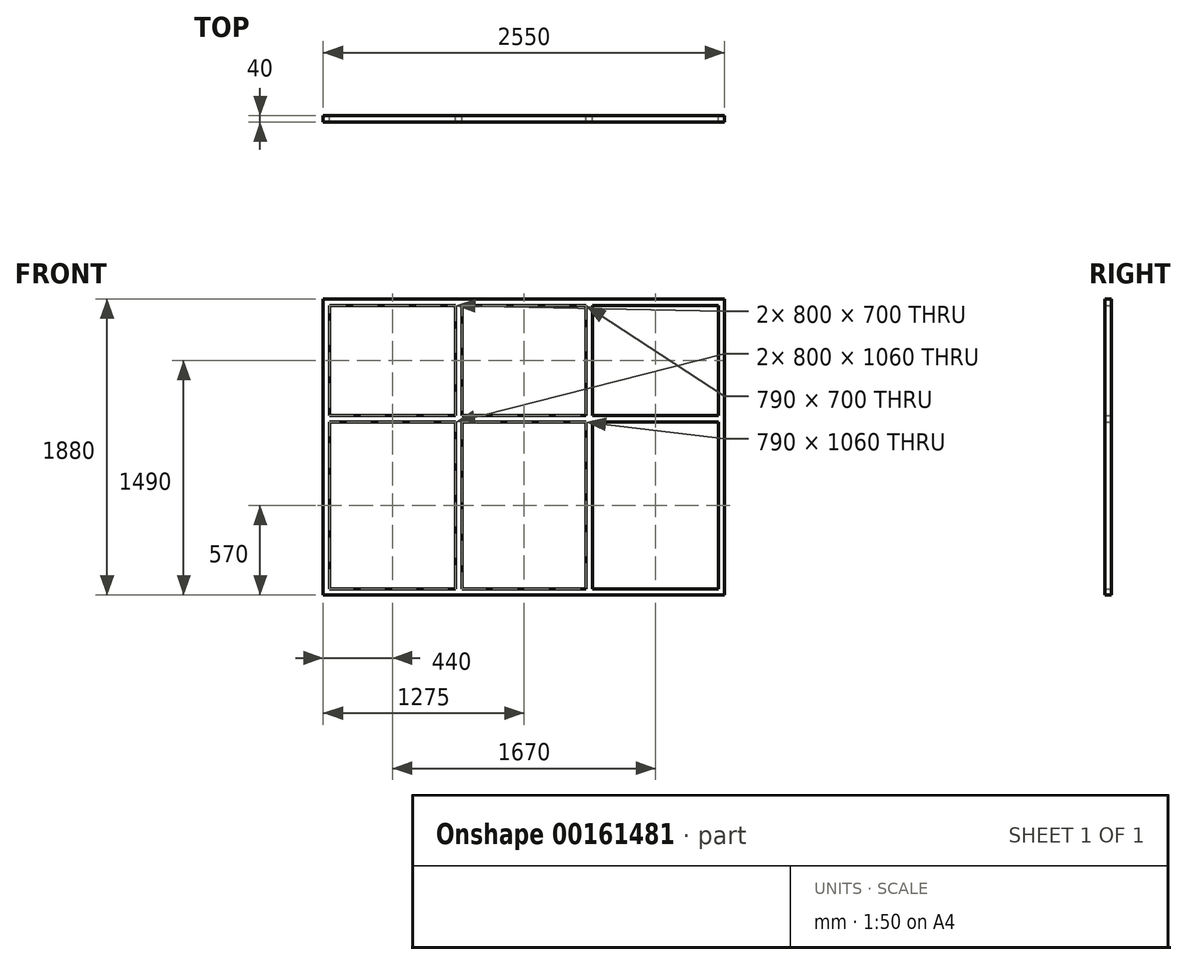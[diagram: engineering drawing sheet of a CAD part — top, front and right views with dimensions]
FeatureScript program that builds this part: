
annotation { "Feature Type Name" : "Feature", "Feature Type Description" : "" }
export const myFeature = defineFeature(function(context is Context, id is Id, definition is map)
    precondition{}
    {
        {
            var Q0;
            Q0=qCreatedBy(makeId("Front.planeOp"),FACE);
            var sketch = newSketch(context, id + "F0", { "sketchPlane" : qUnion([Q0])});
            skLineSegment(sketch, "E0.bottom", {"start": v(-1235, 900) * mm, "end": v(-435, 900) * mm});
            skLineSegment(sketch, "E0.top", {"start": v(-1235, -900) * mm, "end": v(-435, -900) * mm});
            skLineSegment(sketch, "E0.left", {"start": v(-1235, 900) * mm, "end": v(-1235, 200) * mm});
            skLineSegment(sketch, "E0.right", {"start": v(1235, 900) * mm, "end": v(1235, 200) * mm});
            skPoint(sketch, "E0.middle", {"position": v(0, 0) * mm});
            skLineSegment(sketch, "E1.bottom", {"start": v(-1275, 940) * mm, "end": v(1275, 940) * mm});
            skLineSegment(sketch, "E1.top", {"start": v(-1275, -940) * mm, "end": v(1275, -940) * mm});
            skLineSegment(sketch, "E1.left", {"start": v(-1275, 940) * mm, "end": v(-1275, -940) * mm});
            skLineSegment(sketch, "E1.right", {"start": v(1275, 940) * mm, "end": v(1275, -940) * mm});
            skLineSegment(sketch, "E2.left", {"start": v(-435, 900) * mm, "end": v(-435, 200) * mm});
            skLineSegment(sketch, "E2.right", {"start": v(-395, 900) * mm, "end": v(-395, 200) * mm});
            skLineSegment(sketch, "E3.left", {"start": v(395, 900) * mm, "end": v(395, 200) * mm});
            skLineSegment(sketch, "E3.right", {"start": v(435, 900) * mm, "end": v(435, 200) * mm});
            skLineSegment(sketch, "E4.trimOffspring", {"start": v(-395, 900) * mm, "end": v(395, 900) * mm});
            skLineSegment(sketch, "E5.trimOffspring", {"start": v(-395, -900) * mm, "end": v(395, -900) * mm});
            skLineSegment(sketch, "E6.trimOffspring", {"start": v(435, 900) * mm, "end": v(1235, 900) * mm});
            skLineSegment(sketch, "E7.trimOffspring", {"start": v(435, -900) * mm, "end": v(1235, -900) * mm});
            skLineSegment(sketch, "E8.bottom", {"start": v(-1235, 200) * mm, "end": v(-435, 200) * mm});
            skLineSegment(sketch, "E8.top", {"start": v(-1235, 160) * mm, "end": v(-435, 160) * mm});
            skLineSegment(sketch, "E9.trimOffspring", {"start": v(-435, 160) * mm, "end": v(-435, -900) * mm});
            skLineSegment(sketch, "E10.trimOffspring", {"start": v(-1235, 160) * mm, "end": v(-1235, -900) * mm});
            skLineSegment(sketch, "E11", {"start": v(-395, 200) * mm, "end": v(395, 200) * mm});
            skLineSegment(sketch, "E12", {"start": v(-395, 160) * mm, "end": v(395, 160) * mm});
            skLineSegment(sketch, "E13.trimOffspring", {"start": v(-395, 160) * mm, "end": v(-395, -900) * mm});
            skLineSegment(sketch, "E14.trimOffspring", {"start": v(395, 160) * mm, "end": v(395, -900) * mm});
            skLineSegment(sketch, "E15.trimOffspring", {"start": v(435, 200) * mm, "end": v(1235, 200) * mm});
            skLineSegment(sketch, "E16.trimOffspring", {"start": v(435, 160) * mm, "end": v(1235, 160) * mm});
            skLineSegment(sketch, "E17.trimOffspring", {"start": v(435, 160) * mm, "end": v(435, -900) * mm});
            skLineSegment(sketch, "E18.trimOffspring", {"start": v(1235, 160) * mm, "end": v(1235, -900) * mm});
            skSolve(sketch);
        }
        {
            var Q0;
            Q0 = qSketchRegion(id + "F0", true);
            extrude(context, id + "F1", {"entities" : qUnion([Q0]), "endBound" : BoundingType.SYMMETRIC, "depth" : 40 * mm, "offsetDistance" : 25 * mm});
        }
    });
